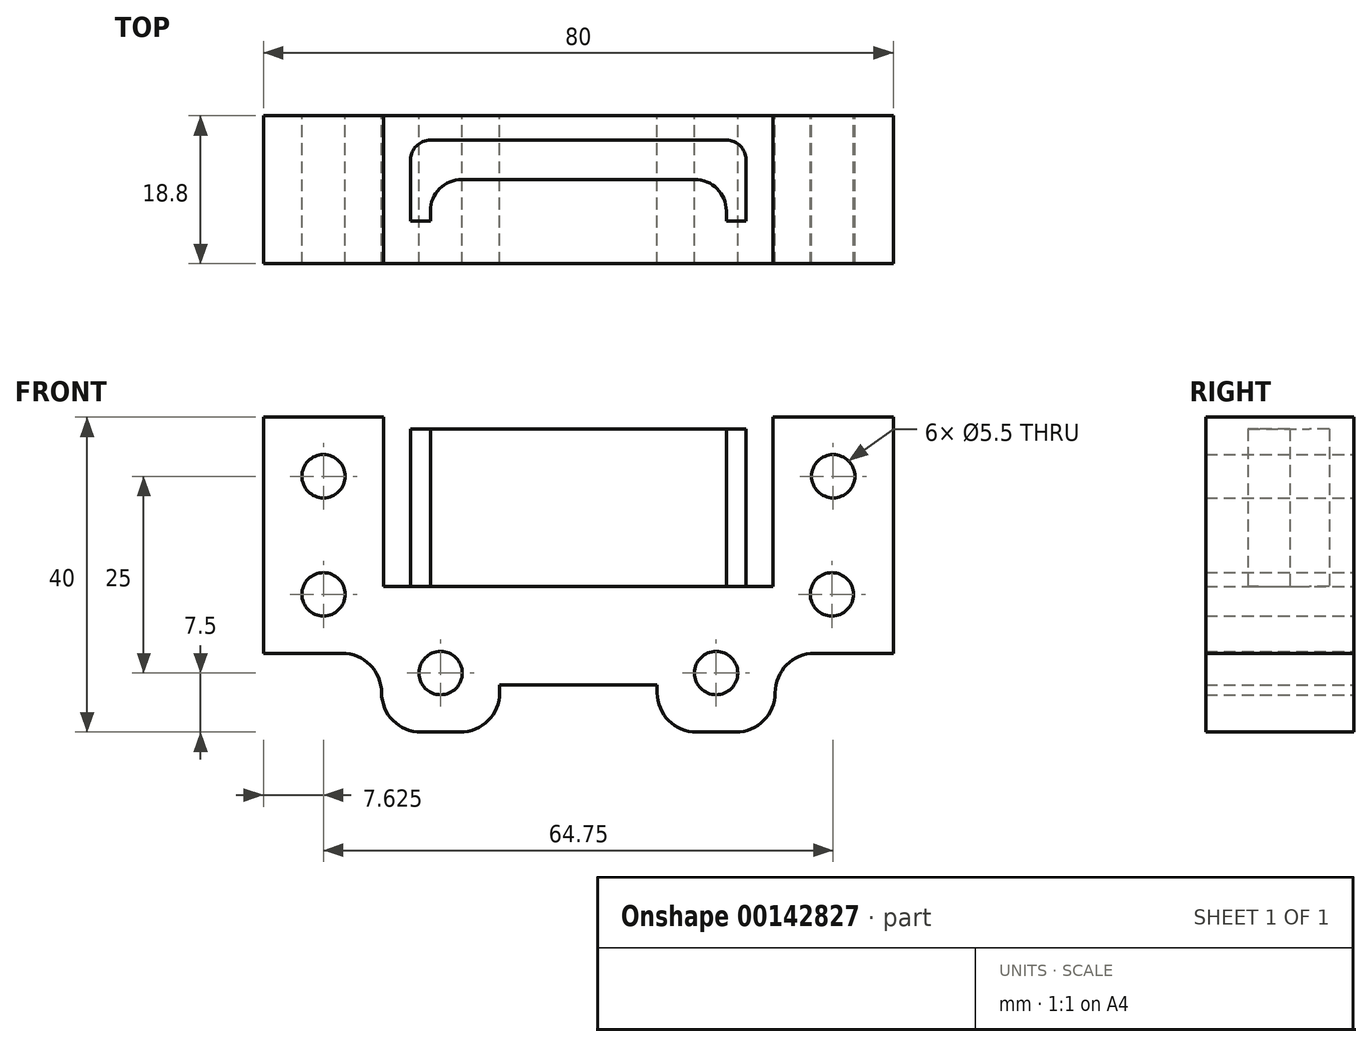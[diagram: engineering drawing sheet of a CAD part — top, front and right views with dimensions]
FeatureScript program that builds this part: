
annotation { "Feature Type Name" : "Feature", "Feature Type Description" : "" }
export const myFeature = defineFeature(function(context is Context, id is Id, definition is map)
    precondition{}
    {
        {
            var Q0;
            Q0=qCreatedBy(makeId("Front.planeOp"),FACE);
            var sketch = newSketch(context, id + "F0", { "sketchPlane" : qUnion([Q0])});
            skLineSegment(sketch, "E0.bottom", {"start": v(-40, 21.5) * mm, "end": v(-24.75, 21.5) * mm});
            skLineSegment(sketch, "E0.top", {"start": v(-25, -18.5) * mm, "end": v(-10, -18.5) * mm});
            skLineSegment(sketch, "E0.left", {"start": v(-40, 21.5) * mm, "end": v(-40, -8.5) * mm});
            skLineSegment(sketch, "E0.right", {"start": v(40, 21.5) * mm, "end": v(40, -8.5) * mm});
            skLineSegment(sketch, "E1.top", {"start": v(-24.75, 0) * mm, "end": v(24.75, 0) * mm});
            skLineSegment(sketch, "E1.left", {"start": v(-24.75, 21.5) * mm, "end": v(-24.75, 0) * mm});
            skLineSegment(sketch, "E1.right", {"start": v(24.75, 21.5) * mm, "end": v(24.75, 0) * mm});
            skLineSegment(sketch, "E2.trimOffspring", {"start": v(24.75, 21.5) * mm, "end": v(40, 21.5) * mm});
            skLineSegment(sketch, "E3", {"start": v(-25, -8.5) * mm, "end": v(-25, -18.5) * mm});
            skLineSegment(sketch, "E4", {"start": v(40, -8.5) * mm, "end": v(25, -8.5) * mm});
            skLineSegment(sketch, "E5", {"start": v(25, -8.5) * mm, "end": v(25, -18.5) * mm});
            skLineSegment(sketch, "E6", {"start": v(-40, -8.5) * mm, "end": v(-25, -8.5) * mm});
            skLineSegment(sketch, "E7.trimOffspring", {"start": v(10, -18.5) * mm, "end": v(25, -18.5) * mm});
            skLineSegment(sketch, "E8.bottom", {"start": v(10, -18.5) * mm, "end": v(10.01, -18.5) * mm});
            skLineSegment(sketch, "E8.top", {"start": v(-10, -12.5) * mm, "end": v(10.01, -12.5) * mm});
            skLineSegment(sketch, "E8.left", {"start": v(-10, -18.5) * mm, "end": v(-10, -12.5) * mm});
            skLineSegment(sketch, "E8.right", {"start": v(10.01, -18.5) * mm, "end": v(10.01, -12.5) * mm});
            skSolve(sketch);
        }
        {
            var Q0;
            Q0=qSketchRegion(id+"F0",true);
            extrude(context, id + "F1", {"entities" : qUnion([Q0]), "depth" : 18.8 * mm, "offsetDistance" : 25 * mm});
        }
        {
            var Q0;
            Q0=makeQuery(id+"F1.opExtrude","SWEPT_FACE",FACE,{"disambiguationData":[OSD([sQuery(id+"F0.wireOp",EDGE,"E1.top")])]});
            var sketch = newSketch(context, id + "F2", { "sketchPlane" : qUnion([Q0])});
            skLineSegment(sketch, "E9.bottom", {"start": v(-21.3, -3.1) * mm, "end": v(21.3, -3.1) * mm});
            skLineSegment(sketch, "E10.0", {"start": v(-18.8, -8.1) * mm, "end": v(18.8, -8.1) * mm});
            skLineSegment(sketch, "E11.0", {"start": v(-21.3, -13.4) * mm, "end": v(-18.8, -13.4) * mm});
            skLineSegment(sketch, "E12", {"start": v(18.8, -8.1) * mm, "end": v(18.8, -13.4) * mm});
            skLineSegment(sketch, "E13.trimOffspring", {"start": v(18.8, -13.4) * mm, "end": v(21.3, -13.4) * mm});
            skPoint(sketch, "E14.orphan", {"position": v(-22.05, -15.9) * mm});
            skLineSegment(sketch, "E15", {"start": v(21.3, -13.4) * mm, "end": v(21.3, -3.1) * mm});
            skLineSegment(sketch, "E16", {"start": v(-21.3, -3.1) * mm, "end": v(-21.3, -13.4) * mm});
            skLineSegment(sketch, "E17", {"start": v(-18.8, -8.1) * mm, "end": v(-18.8, -13.4) * mm});
            skSolve(sketch);
        }
        {
            var Q0;
            Q0=qSketchRegion(id+"F2",true);
            extrude(context, id + "F3", {"entities" : qUnion([Q0]), "depth" : 20 * mm, "offsetDistance" : 25 * mm});
        }
        {
            var Q0;
            Q0=makeQuery(id+"F3.opExtrude","SWEPT_EDGE",EDGE,{"disambiguationData":[OSD([sQuery(id+"F2.wireOp",EDGE,"E10.0"),sQuery(id+"F2.wireOp",EDGE,"E17")])]});
            fillet(context, id + "F4", {"entities" : qUnion([Q0]), "radius" : 4 * mm, "tangentPropagation" : true, "allowEdgeOverflow" : false});
        }
        {
            var Q0;
            Q0=makeQuery(id+"F3.opExtrude","SWEPT_EDGE",EDGE,{"disambiguationData":[OSD([sQuery(id+"F2.wireOp",EDGE,"E9.bottom"),sQuery(id+"F2.wireOp",EDGE,"E15")])]});
            fillet(context, id + "F5", {"entities" : qUnion([Q0]), "radius" : 2.5 * mm, "tangentPropagation" : true, "allowEdgeOverflow" : false});
        }
        {
            var Q0;
            Q0=makeQuery(id+"F3.opExtrude","SWEPT_EDGE",EDGE,{"disambiguationData":[OSD([sQuery(id+"F2.wireOp",EDGE,"E9.bottom"),sQuery(id+"F2.wireOp",EDGE,"E16")])]});
            fillet(context, id + "F6", {"entities" : qUnion([Q0]), "radius" : 2.5 * mm, "tangentPropagation" : true, "allowEdgeOverflow" : false});
        }
        {
            var Q0;
            Q0=makeQuery(id+"F3.opExtrude","SWEPT_EDGE",EDGE,{"disambiguationData":[OSD([sQuery(id+"F2.wireOp",EDGE,"E10.0"),sQuery(id+"F2.wireOp",EDGE,"E12")])]});
            fillet(context, id + "F7", {"entities" : qUnion([Q0]), "radius" : (4) * mm, "tangentPropagation" : true, "allowEdgeOverflow" : false});
        }
        {
            var Q0;
            Q0=makeQuery(id+"F1.opExtrude","SWEPT_EDGE",EDGE,{"disambiguationData":[OSD([sQuery(id+"F0.wireOp",EDGE,"E0.top"),sQuery(id+"F0.wireOp",EDGE,"E3")])]});
            var Q1;
            Q1=makeQuery(id+"F1.opExtrude","SWEPT_EDGE",EDGE,{"disambiguationData":[OSD([sQuery(id+"F0.wireOp",EDGE,"E0.top"),sQuery(id+"F0.wireOp",EDGE,"PGSZPBY5-k11s-mBLS-jqFu-Z2NhK5MSOLEo.left")])]});
            var Q2;
            Q2=makeQuery(id+"F1.opExtrude","SWEPT_EDGE",EDGE,{"disambiguationData":[OSD([sQuery(id+"F0.wireOp",EDGE,"PGSZPBY5-k11s-mBLS-jqFu-Z2NhK5MSOLEo.right"),sQuery(id+"F0.wireOp",EDGE,"E7.trimOffspring")])]});
            var Q3;
            Q3=makeQuery(id+"F1.opExtrude","SWEPT_EDGE",EDGE,{"disambiguationData":[OSD([sQuery(id+"F0.wireOp",EDGE,"E5"),sQuery(id+"F0.wireOp",EDGE,"E7.trimOffspring")])]});
            fillet(context, id + "F8", {"entities" : qUnion([Q0, Q1, Q2, Q3]), "radius" : 5 * mm, "tangentPropagation" : true, "allowEdgeOverflow" : false});
        }
        {
            var Q0;
            Q0=makeQuery(id+"F1.opExtrude","CAP_FACE",FACE,{"disambiguationData":[OSD([sQuery(id+"F0.wireOp",EDGE,"E0.bottom"),sQuery(id+"F0.wireOp",EDGE,"E0.top"),sQuery(id+"F0.wireOp",EDGE,"E0.left"),sQuery(id+"F0.wireOp",EDGE,"E0.right"),sQuery(id+"F0.wireOp",EDGE,"E1.top"),sQuery(id+"F0.wireOp",EDGE,"E1.left"),sQuery(id+"F0.wireOp",EDGE,"E1.right"),sQuery(id+"F0.wireOp",EDGE,"E2.trimOffspring"),sQuery(id+"F0.wireOp",EDGE,"E3"),sQuery(id+"F0.wireOp",EDGE,"E4"),sQuery(id+"F0.wireOp",EDGE,"E5"),sQuery(id+"F0.wireOp",EDGE,"E6"),sQuery(id+"F0.wireOp",EDGE,"PGSZPBY5-k11s-mBLS-jqFu-Z2NhK5MSOLEo.bottom"),sQuery(id+"F0.wireOp",EDGE,"PGSZPBY5-k11s-mBLS-jqFu-Z2NhK5MSOLEo.left"),sQuery(id+"F0.wireOp",EDGE,"PGSZPBY5-k11s-mBLS-jqFu-Z2NhK5MSOLEo.right"),sQuery(id+"F0.wireOp",EDGE,"E7.trimOffspring")])],"isStart":false});
            var sketch = newSketch(context, id + "F9", { "sketchPlane" : qUnion([Q0])});
            skPoint(sketch, "E18", {"position": v(-32.38, 14) * mm});
            skPoint(sketch, "E19", {"position": v(-32.38, -1) * mm});
            skPoint(sketch, "E20", {"position": v(32.38, 14) * mm});
            skPoint(sketch, "E21", {"position": v(32.2, -1) * mm});
            skPoint(sketch, "E22", {"position": v(-17.5, -11) * mm});
            skPoint(sketch, "E23", {"position": v(17.5, -11) * mm});
            skSolve(sketch);
        }
        {
            var Q0;
            Q0=makeQuery(id+"F1.opExtrude","SWEPT_EDGE",EDGE,{"disambiguationData":[OSD([sQuery(id+"F0.wireOp",EDGE,"E3"),sQuery(id+"F0.wireOp",EDGE,"E6")])]});
            fillet(context, id + "F10", {"entities" : qUnion([Q0]), "radius" : 5 * mm, "tangentPropagation" : true, "allowEdgeOverflow" : false});
        }
        {
            var Q0;
            Q0=makeQuery(id+"F1.opExtrude","SWEPT_EDGE",EDGE,{"disambiguationData":[OSD([sQuery(id+"F0.wireOp",EDGE,"E4"),sQuery(id+"F0.wireOp",EDGE,"E5")])]});
            fillet(context, id + "F11", {"entities" : qUnion([Q0]), "radius" : 5 * mm, "tangentPropagation" : true, "allowEdgeOverflow" : false});
        }
        {
            var Q0;
            Q0=sQuery(id+"F9.wireOp",VERTEX,"E18");
            var Q1;
            Q1=sQuery(id+"F9.wireOp",VERTEX,"E19");
            var Q2;
            Q2=sQuery(id+"F9.wireOp",VERTEX,"E22");
            var Q3;
            Q3=sQuery(id+"F9.wireOp",VERTEX,"E23");
            var Q4;
            Q4=sQuery(id+"F9.wireOp",VERTEX,"E21");
            var Q5;
            Q5=sQuery(id+"F9.wireOp",VERTEX,"E20");
            var Q6;
            Q6=makeQuery(id+"F1.opExtrude","SWEPT_BODY",BODY,{"disambiguationData":[OSD([sQuery(id+"F0.wireOp",EDGE,"E0.bottom"),sQuery(id+"F0.wireOp",EDGE,"E0.top"),sQuery(id+"F0.wireOp",EDGE,"E0.left"),sQuery(id+"F0.wireOp",EDGE,"E0.right"),sQuery(id+"F0.wireOp",EDGE,"E1.top"),sQuery(id+"F0.wireOp",EDGE,"E1.left"),sQuery(id+"F0.wireOp",EDGE,"E1.right"),sQuery(id+"F0.wireOp",EDGE,"E2.trimOffspring"),sQuery(id+"F0.wireOp",EDGE,"E3"),sQuery(id+"F0.wireOp",EDGE,"E4"),sQuery(id+"F0.wireOp",EDGE,"E5"),sQuery(id+"F0.wireOp",EDGE,"E6"),sQuery(id+"F0.wireOp",EDGE,"E7.trimOffspring"),sQuery(id+"F0.wireOp",EDGE,"I10cUkJ8-joOk-CUXT-HRMu-5AUbFI4qrsPZ")])]});
            hole(context, id + "F12", {"style" : HoleStyle.SIMPLE, "endStyle" : HoleEndStyle.THROUGH, "holeDiameter" : 5.5 * mm, "majorDiameter" : 5 * mm, "isTappedThrough" : true, "tappedDepth" : 12 * mm, "tapClearance" : 3, "locations" : qUnion([Q0, Q1, Q2, Q3, Q4, Q5]), "scope" : qUnion([Q6]), "startStyle" : HoleStartStyle.SKETCH});
        }
    });
